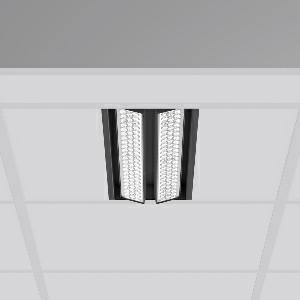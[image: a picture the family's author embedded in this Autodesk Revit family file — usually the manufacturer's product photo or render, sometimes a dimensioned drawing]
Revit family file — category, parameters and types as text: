
# Revit family: tx-move_901732_003_76_d317
name_source: partatom
category: Lighting Fixtures
units: mm (PartAtom-declared; Revit-internal decimal feet)

## family parameters
Cut with Voids When Loaded = No
Host = Face
Light Source = No
Part Type = Normal
Room Calculation Point = No
Round Connector Dimension = Use Diameter
Shared = No

## types (1)
- MultiLumen 1 (1 x LED Modul 830, 2750 lm, 3000)
    Apparent Load = 35 VA
    Approval mark = CE
    CIE Flux Codes = 90 97 99 100 100
    Color Rendering = 80
    Color Temperature = 3000
    Default Elevation = 1800 mm
    Description = Series: TX-MOVE
Einlege/Einbau-Flächenstrahler. Housing: sheet steel, powder-coated. 2xSwivel range: 90°. High-efficiency LED units with optimum light control thanks to clear plastic (PC) lens optics. Spezielle Mikrostrukturen reduzieren Gelbsaum. Symmetrical light distribution. Suitable for laying in grid ceiling module 600. Connected converter included in separate gearbox.Suitable for through-wiring.MultiLumen: Luminous flux adjustable in 3 steps. Accessories: Mounting frame for installation in suspended ceilings. Environmentally friendly and resource-saving due to replaceable and recyclable components. 
Colour: deep black, matt (RAL 9005)
Length: 597 mm
Width: 190 mm
Height: 39 mm
Cut-out length: 577.5 mm
Cut-out width: 174 mm
Recess height: 100 mm
Lamp: LED
Socket: without socket
Colour temperature: 3000K
Colour rendering index (CRI): 80
System power: 35 W
Rated luminous flux: 5500 lm
Luminous efficiency: 157 lm/W
System power 2: 47 W
Rated luminous flux 2: 7100 lm
Luminous efficiency 2: 151 lm/W
System power 3: 68 W
Rated luminous flux 3: 9700 lm
Luminous efficiency 3: 143 lm/W
Control gear: Dimmable EVG, DALI
Protection class: I
Type of protection: IP 20
    Height = 0 mm  [stored 0 ft]
    Lamp = 1 x LED Modul 830
    Lamp Light Flux = 2750 lm
    Lamp count = 1
    Length = 597 mm
    Lifetime = 50000 h
    Luminous efficacy = 157 lm/W
    Manufacturer = RZB
    ModVariant = No
    Model = 901732.003.76
    Mounting Place = Ceiling, Wall
    Mounting Type = Recessed
    Number of Poles = 1
    OnlyDefault = Yes
    Power Factor = 1
    Product Name = TX-MOVE
    Product group = Recessed projectors
    ProductGroupID = 401
    Protection Class = Protection class I
    Protection Degree = IP 20
    RLX_Detail_Level = 1
    RLX_Emergency_Light_Flux = 0 lm
    RLX_Emergency_Type = 0
    RLX_Emergency_Type_DB = No
    RlxData = <blob elided: 36897 chars, md5=a8ec1d27>
    Socket = socket
    Standby Power = 0 W
    System Light Flux = 5500 lm
    System Power = 35 W
    Type Comments = MultiLumen 1
    Type Image = 901733.003.jpg
    URL = http://relux.com
    VarID = multilumen_1
    Voltage = 230 V
    Voltage Range = 220-240 V
    Weight = 0.00 kg
    Width = 190 mm  [stored 0.62336 ft]

note: [stored X ft] marks values corroborated as IEEE doubles in the binary element streams (Revit-internal decimal feet)

## geometry (parser evidence)
native form markers: Blend x4, Sweep x13
no freeform markers — native parametric forms only
